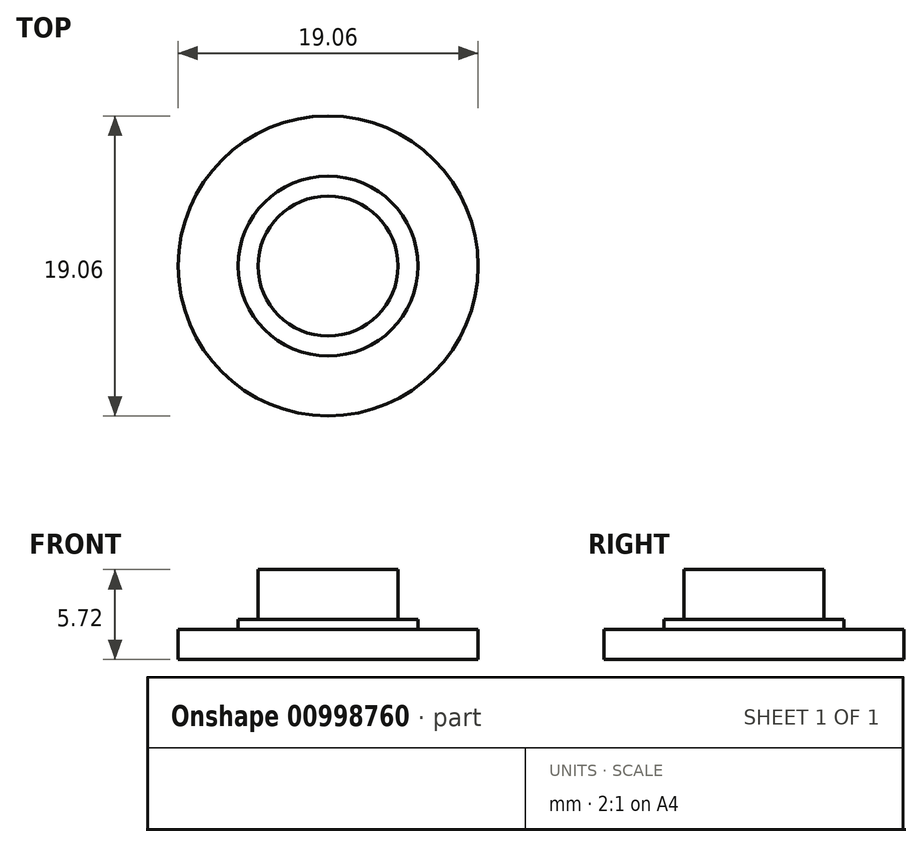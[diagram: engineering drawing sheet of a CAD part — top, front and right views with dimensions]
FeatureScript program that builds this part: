
annotation { "Feature Type Name" : "Feature", "Feature Type Description" : "" }
export const myFeature = defineFeature(function(context is Context, id is Id, definition is map)
    precondition{}
    {
        {
            var Q0;
            Q0=qCreatedBy(makeId("Top.planeOp"),FACE);
            var sketch = newSketch(context, id + "F0", { "sketchPlane" : qUnion([Q0])});
            skCircle(sketch, "E0", {"center": v(0, 0) * mm, "radius": 4.45 * mm});
            skCircle(sketch, "E1", {"center": v(0, 0) * mm, "radius": 9.53 * mm});
            skCircle(sketch, "E2", {"center": v(0, 0) * mm, "radius": 5.72 * mm});
            skSolve(sketch);
        }
        {
            var Q0;
            Q0=makeQuery(id+"F0.imprint","IMPRINT",FACE,{"disambiguationData":[TD([[makeQuery(id+"F0.imprint","IMPRINT",EDGE,{"derivedFrom":sQuery(id+"F0.wireOp",EDGE,"E0")}),1.0]])]});
            extrude(context, id + "F1", {"entities" : qUnion([Q0]), "depth" : 3.17 * mm, "offsetDistance" : 25.4 * mm});
        }
        {
            var Q0;
            Q0=makeQuery(id+"F0.imprint","IMPRINT",FACE,{"disambiguationData":[TD([[makeQuery(id+"F0.imprint","IMPRINT",EDGE,{"derivedFrom":sQuery(id+"F0.wireOp",EDGE,"E0")}),-1.0]])]});
            var Q1;
            Q1=makeQuery(id+"F0.imprint","IMPRINT",FACE,{"disambiguationData":[TD([[makeQuery(id+"F0.imprint","IMPRINT",EDGE,{"derivedFrom":sQuery(id+"F0.wireOp",EDGE,"E0")}),1.0]])]});
            extrude(context, id + "F2", {"entities" : qUnion([Q0, Q1]), "operationType" : NewBodyOperationType.ADD, "oppositeDirection" : true, "depth" : 0.64 * mm, "offsetDistance" : 25.4 * mm});
        }
        {
            var Q0;
            Q0=makeQuery(id+"F0.imprint","IMPRINT",FACE,{"disambiguationData":[TD([[makeQuery(id+"F0.imprint","IMPRINT",EDGE,{"derivedFrom":sQuery(id+"F0.wireOp",EDGE,"E1")}),1.0]])]});
            var Q1;
            Q1=makeQuery(id+"F0.imprint","IMPRINT",FACE,{"disambiguationData":[TD([[makeQuery(id+"F0.imprint","IMPRINT",EDGE,{"derivedFrom":sQuery(id+"F0.wireOp",EDGE,"E0")}),-1.0]])]});
            var Q2;
            Q2=makeQuery(id+"F0.imprint","IMPRINT",FACE,{"disambiguationData":[TD([[makeQuery(id+"F0.imprint","IMPRINT",EDGE,{"derivedFrom":sQuery(id+"F0.wireOp",EDGE,"E0")}),1.0]])]});
            var Q3;
            Q3=makeQuery(id+"F2.opExtrude","CAP_FACE",FACE,{"disambiguationData":[OSD([sQuery(id+"F0.wireOp",EDGE,"E2")])],"isStart":false});
            extrude(context, id + "F3", {"entities" : qUnion([Q0, Q1, Q2]), "operationType" : NewBodyOperationType.ADD, "oppositeDirection" : true, "depth" : 2.54 * mm, "offsetDistance" : 25.4 * mm, "hasSecondDirection" : true, "secondDirectionBound" : SecondDirectionBoundingType.UP_TO_SURFACE, "secondDirectionOppositeDirection" : true, "secondDirectionDepth" : 25.4 * mm, "secondDirectionBoundEntityFace" : qUnion([Q3])});
        }
    });
